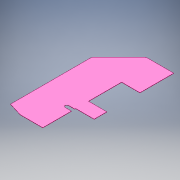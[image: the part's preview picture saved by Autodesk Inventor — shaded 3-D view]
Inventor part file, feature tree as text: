
AUTODESK INVENTOR PART (.ipt)
format: ipt  version: 2018 (Build 220112000, 112)  size: 151,040 bytes
history: native  units: mm
features: extrude x1, fillet x1, sketch x1
ambient origin geometry x8: Origin, YZ Plane, XZ Plane, XY Plane, X Axis, Y Axis, Z Axis, Center Point
bodies: Solid1 (feature_tree)
feature tree (3):
  extrude  "Extrusion1"  Depth=30.0mm
  fillet  "Fillet1"  Radius=800.0mm
  sketch  "Sketch1"  dims[d0=159.0mm d3=100.0mm d6=800.0mm d7=240.0mm d8=130.0mm d11=235.0mm d12=1.6mm d13=0.0mm d14=25.0mm d16=216.0mm d17=0.0mm d18=45.0mm d19=389.0mm d22=130.0mm d23=235.0mm d25=30.0mm d26=270.0mm d27=135.0deg d28=30.0mm]
